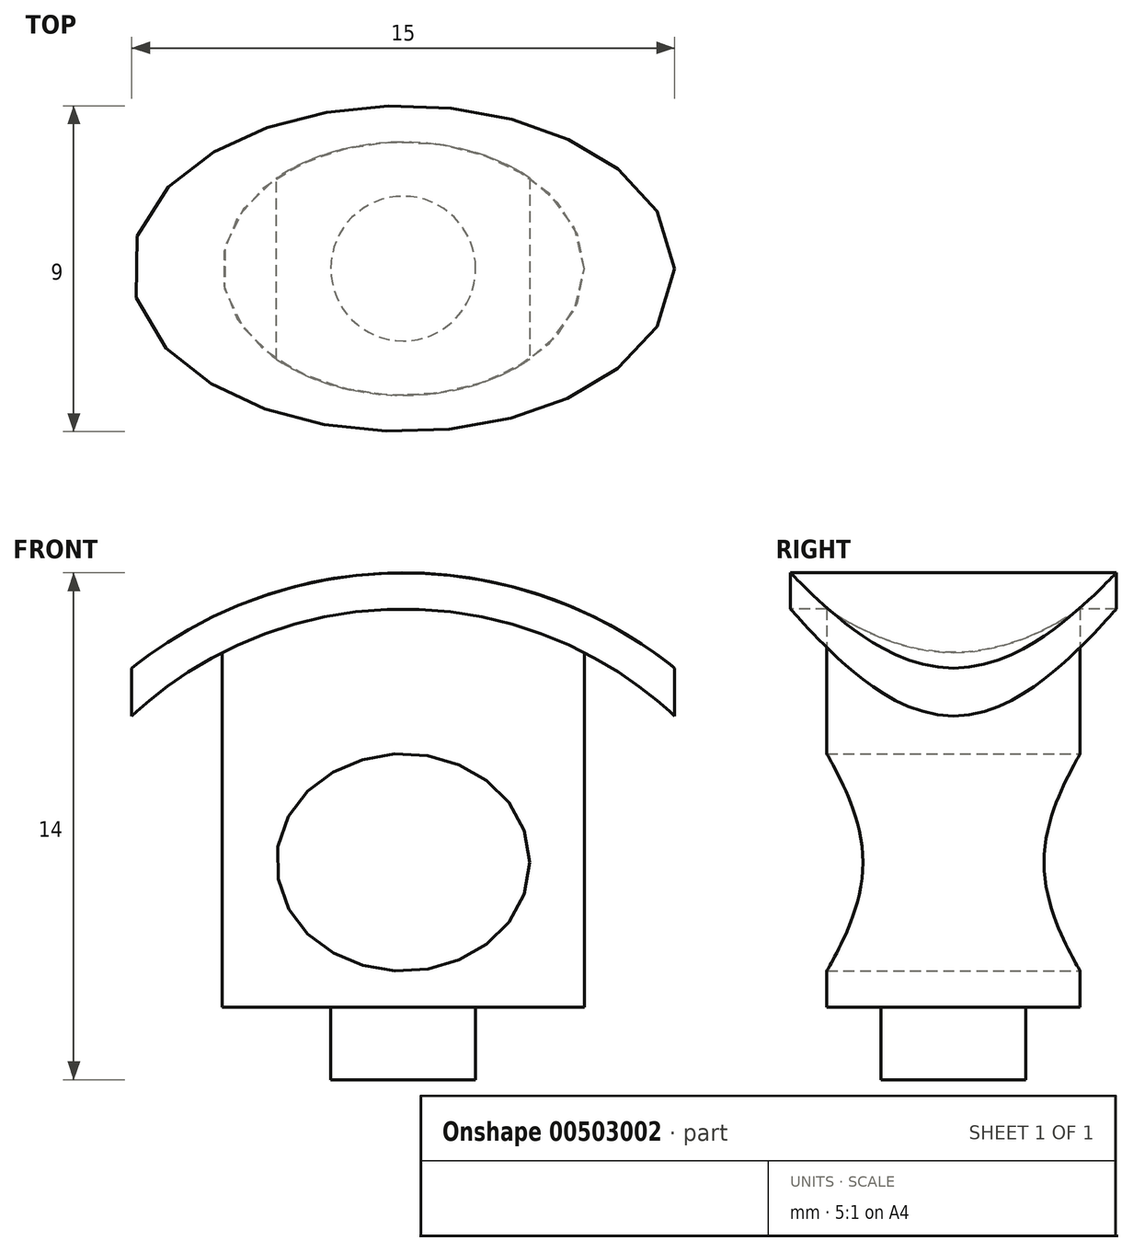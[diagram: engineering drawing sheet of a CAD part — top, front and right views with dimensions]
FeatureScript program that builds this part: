
annotation { "Feature Type Name" : "Feature", "Feature Type Description" : "" }
export const myFeature = defineFeature(function(context is Context, id is Id, definition is map)
    precondition{}
    {
        {
            var Q0;
            Q0=qCreatedBy(makeId("Top.planeOp"),FACE);
            var sketch = newSketch(context, id + "F0", { "sketchPlane" : qUnion([Q0])});
            skEllipse(sketch, "E0", {"center": v(0, 0) * mm, "majorRadius": 7.5 * mm, "minorRadius": 4.5 * mm, "majorAxis": v(1, 0)});
            skSolve(sketch);
        }
        {
            var Q0;
            Q0 = qSketchRegion(id + "F0", true);
            extrude(context, id + "F1", {"entities" : qUnion([Q0]), "depth" : 18.2 * mm});
        }
        {
            var Q0;
            Q0=qCreatedBy(makeId("Front.planeOp"),FACE);
            var sketch = newSketch(context, id + "F2", { "sketchPlane" : qUnion([Q0])});
            skCircle(sketch, "E1", {"center": v(0, 0) * mm, "radius": 12 * mm});
            skCircle(sketch, "E2", {"center": v(0, 0) * mm, "radius": 11 * mm});
            skCircle(sketch, "E3", {"center": v(0, 0) * mm, "radius": 24.45 * mm});
            skSolve(sketch);
        }
        {
            var Q0;
            Q0=makeQuery(id+"F2.imprint","IMPRINT",FACE,{"disambiguationData":[TD([[makeQuery(id+"F2.imprint","IMPRINT",EDGE,{"derivedFrom":sQuery(id+"F2.wireOp",EDGE,"E1")}),-1.0]])]});
            var Q1;
            Q1=makeQuery(id+"F2.imprint","IMPRINT",FACE,{"disambiguationData":[TD([[makeQuery(id+"F2.imprint","IMPRINT",EDGE,{"derivedFrom":sQuery(id+"F2.wireOp",EDGE,"E2")}),1.0]])]});
            extrude(context, id + "F3", {"entities" : qUnion([Q0, Q1]), "operationType" : NewBodyOperationType.REMOVE, "endBound" : BoundingType.SYMMETRIC, "oppositeDirection" : true, "depth" : 25 * mm});
        }
        {
            var Q0;
            Q0=qCreatedBy(makeId("Top.planeOp"),FACE);
            var sketch = newSketch(context, id + "F4", { "sketchPlane" : qUnion([Q0])});
            skEllipse(sketch, "E4", {"center": v(0, 0) * mm, "majorRadius": 5 * mm, "minorRadius": 3.5 * mm, "majorAxis": v(1, 0)});
            skSolve(sketch);
        }
        {
            var Q0;
            Q0 = qSketchRegion(id + "F4", true);
            var Q1;
            Q1=makeQuery(id+"F3.boolean.opBoolean","COPY",FACE,{"derivedFrom":makeQuery(id+"F3.opExtrude","SWEPT_FACE",FACE,{"disambiguationData":[OSD([sQuery(id+"F2.wireOp",EDGE,"E2")])]})});
            extrude(context, id + "F5", {"entities" : qUnion([Q0]), "operationType" : NewBodyOperationType.ADD, "endBound" : BoundingType.UP_TO_SURFACE, "endBoundEntityFace" : qUnion([Q1]), "depth" : 25 * mm});
        }
        {
            var Q0;
            Q0=makeQuery(id+"F5.opExtrude","CAP_FACE",FACE,{"disambiguationData":[OSD([sQuery(id+"F4.wireOp",EDGE,"E4")])],"isStart":true});
            var sketch = newSketch(context, id + "F6", { "sketchPlane" : qUnion([Q0])});
            skCircle(sketch, "E5", {"center": v(0, 0) * mm, "radius": 2 * mm});
            skSolve(sketch);
        }
        {
            var Q0;
            Q0 = qSketchRegion(id + "F6", true);
            extrude(context, id + "F7", {"entities" : qUnion([Q0]), "operationType" : NewBodyOperationType.ADD, "depth" : 2 * mm});
        }
        {
            var Q0;
            Q0=qCreatedBy(makeId("Front.planeOp"),FACE);
            var sketch = newSketch(context, id + "F8", { "sketchPlane" : qUnion([Q0])});
            skEllipse(sketch, "E6", {"center": v(0, 4) * mm, "majorRadius": 3.5 * mm, "minorRadius": 3 * mm, "majorAxis": v(1, 0)});
            skSolve(sketch);
        }
        {
            var Q0;
            Q0 = qSketchRegion(id + "F8", true);
            extrude(context, id + "F9", {"entities" : qUnion([Q0]), "operationType" : NewBodyOperationType.REMOVE, "endBound" : BoundingType.SYMMETRIC, "oppositeDirection" : true, "depth" : 25 * mm});
        }
    });
